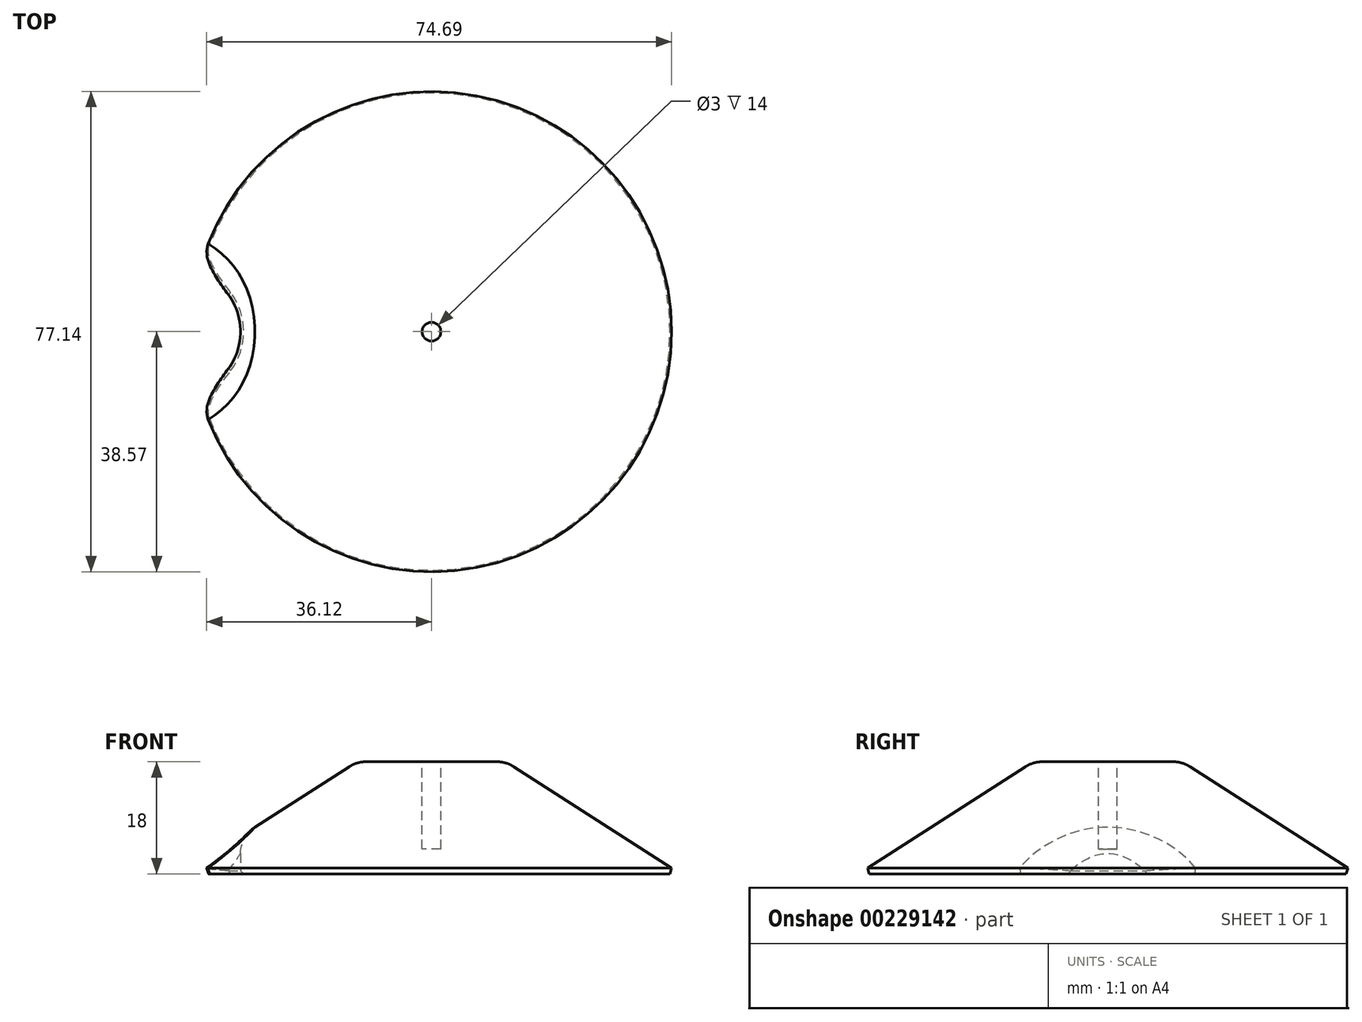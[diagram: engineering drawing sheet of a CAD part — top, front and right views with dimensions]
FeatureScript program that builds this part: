
annotation { "Feature Type Name" : "Feature", "Feature Type Description" : "" }
export const myFeature = defineFeature(function(context is Context, id is Id, definition is map)
    precondition{}
    {
        {
            var Q0;
            Q0=qCreatedBy(makeId("Front.planeOp"),FACE);
            var sketch = newSketch(context, id + "F0", { "sketchPlane" : qUnion([Q0])});
            skLineSegment(sketch, "E0", {"start": v(0, 0) * mm, "end": v(-40, 0) * mm});
            skLineSegment(sketch, "E1", {"start": v(-40, 0) * mm, "end": v(-12, 18) * mm});
            skLineSegment(sketch, "E2", {"start": v(-12, 18) * mm, "end": v(0, 18) * mm});
            skLineSegment(sketch, "E3", {"start": v(0, 18) * mm, "end": v(0, 0) * mm});
            skLineSegment(sketch, "E4", {"start": v(0, 58.77) * mm, "end": v(0, -38.03) * mm, "construction": true});
            skSolve(sketch);
        }
        {
            var Q0;
            Q0 = qSketchRegion(id + "F0", true);
            var Q1;
            Q1=sQuery(id+"F0.wireOp",EDGE,"E4");
            revolve(context, id + "F1", {"entities" : qUnion([Q0]), "axis" : qUnion([Q1]), "revolveType" : RevolveType.FULL});
        }
        {
            var Q0;
            Q0=makeQuery(id+"F1.opRevolve","SWEPT_FACE",FACE,{"disambiguationData":[OSD([sQuery(id+"F0.wireOp",EDGE,"E2")])]});
            var sketch = newSketch(context, id + "F2", { "sketchPlane" : qUnion([Q0])});
            skCircle(sketch, "E5", {"center": v(0, 0) * mm, "radius": 1.5 * mm});
            skSolve(sketch);
        }
        {
            var Q0;
            Q0 = qSketchRegion(id + "F2", true);
            extrude(context, id + "F3", {"entities" : qUnion([Q0]), "operationType" : NewBodyOperationType.REMOVE, "oppositeDirection" : true, "depth" : 14 * mm});
        }
        {
            var Q0;
            Q0=qCreatedBy(makeId("Top.planeOp"),FACE);
            var sketch = newSketch(context, id + "F4", { "sketchPlane" : qUnion([Q0])});
            skCircle(sketch, "E6", {"center": v(-40.7, 0) * mm, "radius": 10.03 * mm});
            skSolve(sketch);
        }
        {
            var Q0;
            Q0 = qSketchRegion(id + "F4", true);
            extrude(context, id + "F5", {"entities" : qUnion([Q0]), "operationType" : NewBodyOperationType.REMOVE, "depth" : 25 * mm});
        }
        {
            var Q0;
            Q0=makeQuery(id+"F5.boolean.opBoolean","INTERSECT",EDGE,{"derivedFrom":[makeQuery(id+"F1.opRevolve","SWEPT_FACE",FACE,{"disambiguationData":[OSD([sQuery(id+"F0.wireOp",EDGE,"E1")])]}),makeQuery(id+"F5.opExtrude","SWEPT_FACE",FACE,{"disambiguationData":[OSD([sQuery(id+"F4.wireOp",EDGE,"E6")])]})]});
            var Q1;
            Q1=makeQuery(id+"FDihpTrIaAh2WM0_1.1.F5.boolean.opBoolean","INTERSECT",EDGE,{"derivedFrom":[makeQuery(id+"F1.opRevolve","SWEPT_FACE",FACE,{"disambiguationData":[OSD([sQuery(id+"F0.wireOp",EDGE,"E1")])]}),makeQuery(id+"FDihpTrIaAh2WM0_1.1.F5.opExtrude","SWEPT_FACE",FACE,{"disambiguationData":[OSD([sQuery(id+"F4.wireOp",EDGE,"E6")])]})]});
            var Q2;
            Q2=makeQuery(id+"FDihpTrIaAh2WM0_1.2.F5.boolean.opBoolean","INTERSECT",EDGE,{"derivedFrom":[makeQuery(id+"F1.opRevolve","SWEPT_FACE",FACE,{"disambiguationData":[OSD([sQuery(id+"F0.wireOp",EDGE,"E1")])]}),makeQuery(id+"FDihpTrIaAh2WM0_1.2.F5.opExtrude","SWEPT_FACE",FACE,{"disambiguationData":[OSD([sQuery(id+"F4.wireOp",EDGE,"E6")])]})]});
            var Q3;
            Q3=makeQuery(id+"FDihpTrIaAh2WM0_1.3.F5.boolean.opBoolean","INTERSECT",EDGE,{"derivedFrom":[makeQuery(id+"F1.opRevolve","SWEPT_FACE",FACE,{"disambiguationData":[OSD([sQuery(id+"F0.wireOp",EDGE,"E1")])]}),makeQuery(id+"FDihpTrIaAh2WM0_1.3.F5.opExtrude","SWEPT_FACE",FACE,{"disambiguationData":[OSD([sQuery(id+"F4.wireOp",EDGE,"E6")])]})]});
            var Q4;
            Q4=makeQuery(id+"FDihpTrIaAh2WM0_1.4.F5.boolean.opBoolean","INTERSECT",EDGE,{"derivedFrom":[makeQuery(id+"F1.opRevolve","SWEPT_FACE",FACE,{"disambiguationData":[OSD([sQuery(id+"F0.wireOp",EDGE,"E1")])]}),makeQuery(id+"FDihpTrIaAh2WM0_1.4.F5.opExtrude","SWEPT_FACE",FACE,{"disambiguationData":[OSD([sQuery(id+"F4.wireOp",EDGE,"E6")])]})]});
            var Q5;
            Q5=makeQuery(id+"FDihpTrIaAh2WM0_1.5.F5.boolean.opBoolean","INTERSECT",EDGE,{"derivedFrom":[makeQuery(id+"F1.opRevolve","SWEPT_FACE",FACE,{"disambiguationData":[OSD([sQuery(id+"F0.wireOp",EDGE,"E1")])]}),makeQuery(id+"FDihpTrIaAh2WM0_1.5.F5.opExtrude","SWEPT_FACE",FACE,{"disambiguationData":[OSD([sQuery(id+"F4.wireOp",EDGE,"E6")])]})]});
            var Q6;
            Q6=makeQuery(id+"F1.opRevolve","SWEPT_EDGE",EDGE,{"disambiguationData":[OSD([sQuery(id+"F0.wireOp",EDGE,"E1"),sQuery(id+"F0.wireOp",EDGE,"E2")])]});
            fillet(context, id + "F6", {"entities" : qUnion([Q0, Q1, Q2, Q3, Q4, Q5, Q6]), "radius" : 5 * mm, "tangentPropagation" : true, "allowEdgeOverflow" : false});
        }
        {
            var Q0;
            Q0=makeQuery(id+"F1.opRevolve","SWEPT_FACE",FACE,{"disambiguationData":[OSD([sQuery(id+"F0.wireOp",EDGE,"E0")])]});
            chamfer(context, id + "F7", {"entities" : qUnion([Q0]), "width" : .5 * mm, "tangentPropagation" : true});
        }
    });
